# Revit family: Faucet-Two_Handle-American Standard-Monterrey-750X1X0_Series.rfaxxx
name_source: partatom
category: Plumbing Fixtures
units: mm (PartAtom-declared; Revit-internal decimal feet)

## family parameters
Always vertical = No
Cut with Voids When Loaded = No
OmniClass Number = 23.45.55.17
OmniClass Title = Mixing Faucets
Part Type = Normal
Room Calculation Point = No
Round Connector Dimension = Use Diameter
Shared = Yes
Work Plane-Based = No

## types (3) — shared parameters
ADA Compliant = Yes
Assembly Code = D2020300
CW Connection = Yes
CWFU = 1.5
Cold Water Connection Diameter = 1/2"
Drain/Strainer Depth = 5"
Drain/Strainer Distance from Faucet Centre = 6 1/2"
Finish = Cast Brass-American Standard-002-Polished Chrome
Flow Rate = 1.5 gpm/5.7 Lpm
HW Connection = Yes
HWFU = 1.5
Height = 10 3/4"
Hot Water Connection Diameter = 1/2"
IAPMO Compliance = ASME A112.18.1, CSA B 125, NSF 372 and EPA WaterSense
Installation Type = Deck Mounted
Manufacturer = American Standard
Material = Cast Brass-American Standard-002-Polished Chrome
Price = Prices may vary. Please consult Manufacturer Representative for most up-to-date price list.
Product Documentation Link = https://americanstandard.box.com
Product Page URL = https://www.americanstandard-us.com
Revised Date = 07/25/2022
URL = http://www.americanstandard-us.com
Vent Connection = No
Warranty Information = 5 Year Limited Warranty
Waste Connection = No
zero-valued in all types: WFU

## per-type parameters (varying)
| type | Description | Lever Handles | Metal Grid Strainer | No Drain and Strainer | Width | Wrist Blade Handles |
| 7500.170.002 | Monterrey® 4-Inch Centerset Gooseneck Faucet With Wrist Blade Handles 1.5 gpm/5.7 Lpm | No | No | Yes | 11 3/4" | Yes |
| 7502.170.002 | Monterrey® 4-Inch Centerset Gooseneck Faucet With Lever Handles 1.5 gpm/5.7 Lpm With Grid Drain | No | Yes | No | 11 3/4" | Yes |
| 7500.140.002 | Monterrey® 4-Inch Centerset Gooseneck Faucet With Lever Handles 1.5 gpm/5.7 Lpm | Yes | No | Yes | 8 1/2" | No |

note: column(s) folded — value = type name in every type: Model

## geometry (parser evidence)
native form markers: Sweep x2
no freeform markers — native parametric forms only
